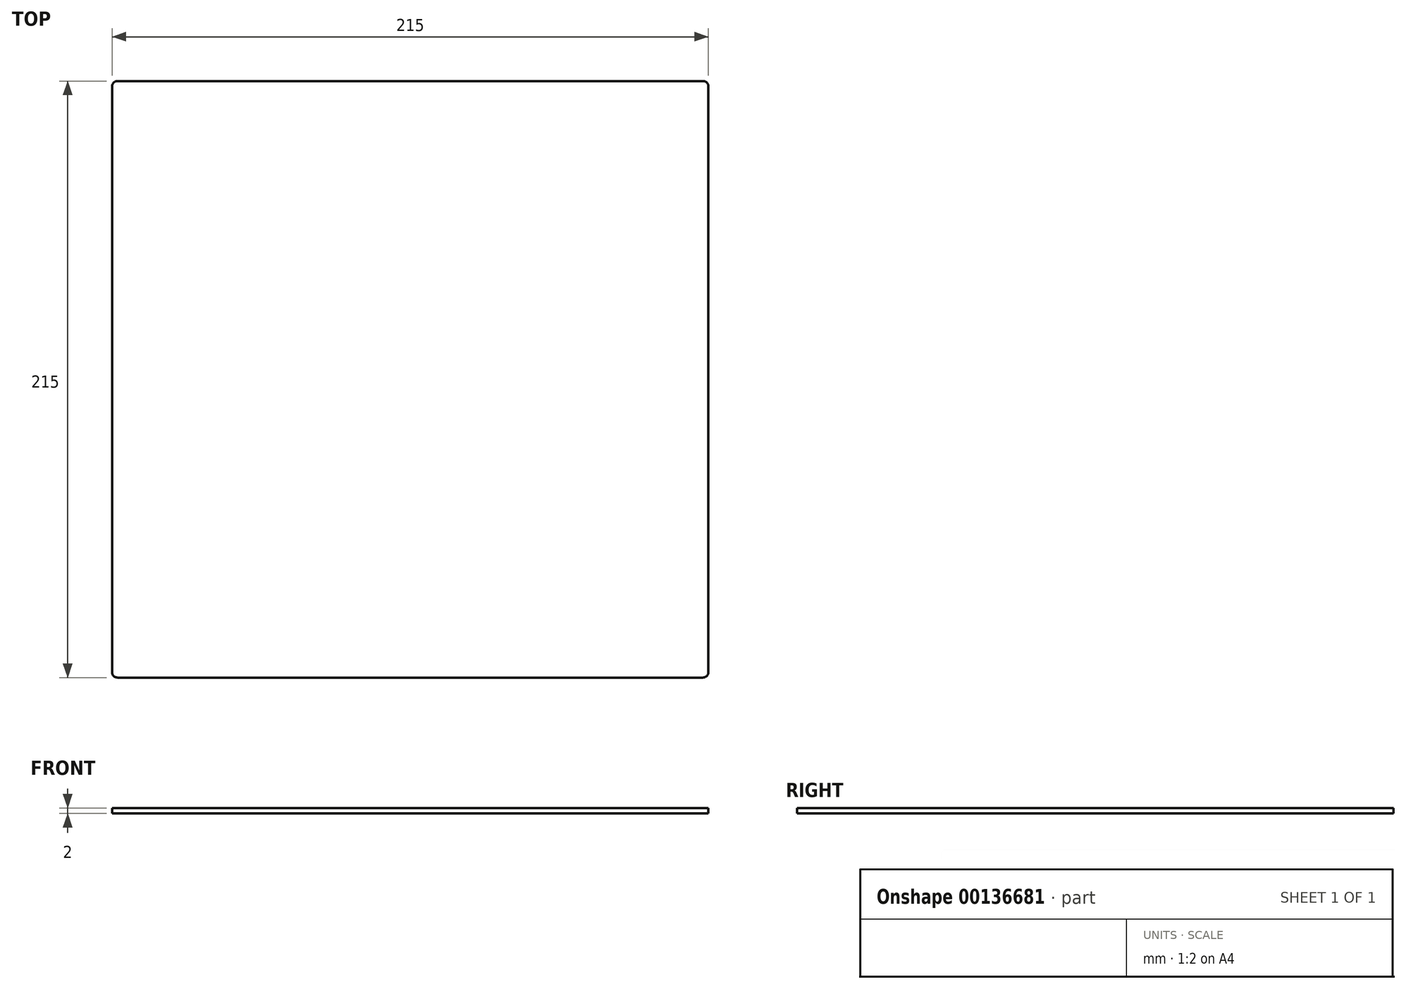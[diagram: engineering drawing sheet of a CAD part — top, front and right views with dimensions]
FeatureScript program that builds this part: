
annotation { "Feature Type Name" : "Feature", "Feature Type Description" : "" }
export const myFeature = defineFeature(function(context is Context, id is Id, definition is map)
    precondition{}
    {
        {
            var Q0;
            Q0=qCreatedBy(makeId("Top.planeOp"),FACE);
            var sketch = newSketch(context, id + "F0", { "sketchPlane" : qUnion([Q0])});
            skLineSegment(sketch, "E0.bottom", {"start": v(-107.5, 107.5) * mm, "end": v(107.5, 107.5) * mm});
            skLineSegment(sketch, "E0.top", {"start": v(-107.5, -107.5) * mm, "end": v(107.5, -107.5) * mm});
            skLineSegment(sketch, "E0.left", {"start": v(-107.5, 107.5) * mm, "end": v(-107.5, -107.5) * mm});
            skLineSegment(sketch, "E0.right", {"start": v(107.5, 107.5) * mm, "end": v(107.5, -107.5) * mm});
            skPoint(sketch, "E0.middle", {"position": v(0, 0) * mm});
            skSolve(sketch);
        }
        {
            var Q0;
            Q0=makeQuery(id+"F0.imprint","IMPRINT",FACE,{"disambiguationData":[TD([[makeQuery(id+"F0.imprint","IMPRINT",EDGE,{"derivedFrom":sQuery(id+"F0.wireOp",EDGE,"E0.bottom")}),-1.0]])]});
            extrude(context, id + "F1", {"entities" : qUnion([Q0]), "depth" : 2 * mm});
        }
        {
            var Q0;
            Q0=makeQuery(id+"F1.opExtrude","SWEPT_EDGE",EDGE,{"disambiguationData":[OSD([sQuery(id+"F0.wireOp",EDGE,"E0.top"),sQuery(id+"F0.wireOp",EDGE,"E0.left")])]});
            var Q1;
            Q1=makeQuery(id+"F1.opExtrude","SWEPT_EDGE",EDGE,{"disambiguationData":[OSD([sQuery(id+"F0.wireOp",EDGE,"E0.top"),sQuery(id+"F0.wireOp",EDGE,"E0.right")])]});
            var Q2;
            Q2=makeQuery(id+"F1.opExtrude","SWEPT_EDGE",EDGE,{"disambiguationData":[OSD([sQuery(id+"F0.wireOp",EDGE,"E0.bottom"),sQuery(id+"F0.wireOp",EDGE,"E0.right")])]});
            var Q3;
            Q3=makeQuery(id+"F1.opExtrude","SWEPT_EDGE",EDGE,{"disambiguationData":[OSD([sQuery(id+"F0.wireOp",EDGE,"E0.bottom"),sQuery(id+"F0.wireOp",EDGE,"E0.left")])]});
            fillet(context, id + "F2", {"entities" : qUnion([Q0, Q1, Q2, Q3]), "radius" : 2 * mm, "tangentPropagation" : true, "allowEdgeOverflow" : false});
        }
    });
